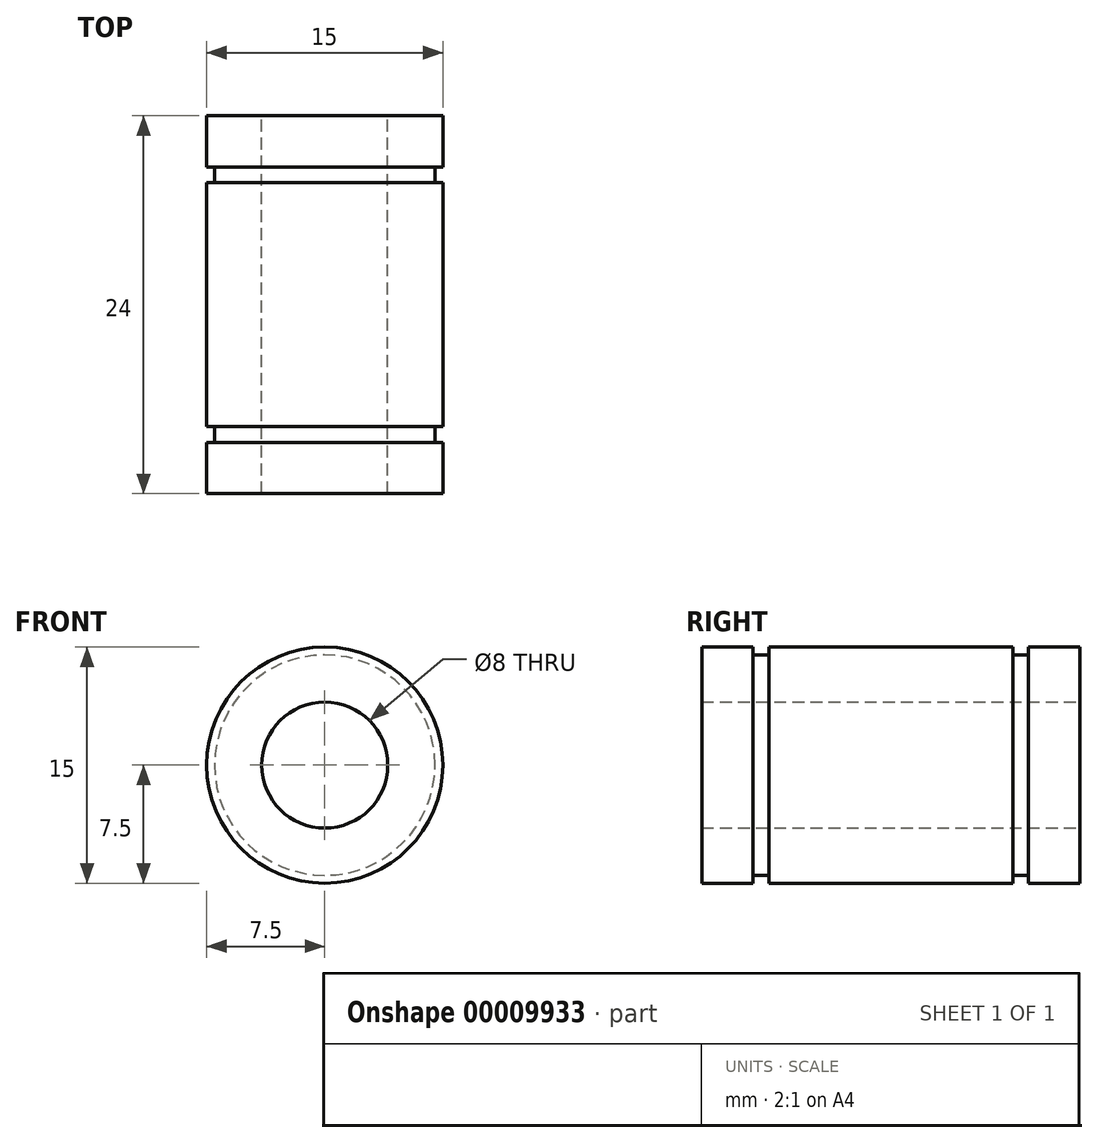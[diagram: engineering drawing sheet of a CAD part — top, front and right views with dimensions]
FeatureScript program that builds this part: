
annotation { "Feature Type Name" : "Feature", "Feature Type Description" : "" }
export const myFeature = defineFeature(function(context is Context, id is Id, definition is map)
    precondition{}
    {
        {
            var Q0;
            Q0=qCreatedBy(makeId("Front.planeOp"),FACE);
            var sketch = newSketch(context, id + "F0", { "sketchPlane" : qUnion([Q0])});
            skCircle(sketch, "E0", {"center": v(0, 0) * mm, "radius": 7.5 * mm});
            skCircle(sketch, "E1", {"center": v(0, 0) * mm, "radius": 4 * mm});
            skSolve(sketch);
        }
        {
            var Q0;
            Q0=qSketchRegion(id+"F0",true);
            extrude(context, id + "F1", {"entities" : qUnion([Q0]), "depth" : 3.25 * mm});
        }
        {
            var Q0;
            Q0=makeQuery(id+"F1.opExtrude","CAP_FACE",FACE,{"disambiguationData":[OSD([sQuery(id+"F0.wireOp",EDGE,"E0"),sQuery(id+"F0.wireOp",EDGE,"E1")])],"isStart":false});
            var sketch = newSketch(context, id + "F2", { "sketchPlane" : qUnion([Q0])});
            skCircle(sketch, "E2", {"center": v(0, 0) * mm, "radius": 7 * mm});
            skSolve(sketch);
        }
        {
            var Q0;
            Q0=makeQuery(id+"F2.imprint","IMPRINT",FACE,{"disambiguationData":[TD([[makeQuery(id+"F2.imprint","IMPRINT",EDGE,{"derivedFrom":sQuery(id+"F2.wireOp",EDGE,"E2")}),1.0]])]});
            extrude(context, id + "F3", {"entities" : qUnion([Q0]), "operationType" : NewBodyOperationType.ADD, "depth" : 1 * mm});
        }
        {
            var Q0;
            Q0=makeQuery(id+"F3.opExtrude","CAP_FACE",FACE,{"disambiguationData":[OSD([sQuery(id+"F0.wireOp",EDGE,"E1"),sQuery(id+"F2.wireOp",EDGE,"E2")])],"isStart":false});
            var sketch = newSketch(context, id + "F4", { "sketchPlane" : qUnion([Q0])});
            skCircle(sketch, "E3.0", {"center": v(0, 0) * mm, "radius": 7.5 * mm});
            skSolve(sketch);
        }
        {
            var Q0;
            Q0=makeQuery(id+"F4.imprint","IMPRINT",FACE,{"disambiguationData":[TD([[makeQuery(id+"F4.imprint","IMPRINT",EDGE,{"derivedFrom":makeQuery(id+"F3.opExtrude","CAP_EDGE",EDGE,{"disambiguationData":[OSD([sQuery(id+"F2.wireOp",EDGE,"E2")])],"isStart":false})}),1.0]])]});
            var Q1;
            Q1=makeQuery(id+"F4.imprint","IMPRINT",FACE,{"disambiguationData":[TD([[makeQuery(id+"F4.imprint","IMPRINT",EDGE,{"derivedFrom":sQuery(id+"F4.wireOp",EDGE,"E3.0")}),1.0]])]});
            extrude(context, id + "F5", {"entities" : qUnion([Q0, Q1]), "operationType" : NewBodyOperationType.ADD, "depth" : 15.5 * mm});
        }
        {
            var Q0;
            Q0=makeQuery(id+"F5.opExtrude","CAP_FACE",FACE,{"disambiguationData":[OSD([sQuery(id+"F0.wireOp",EDGE,"E1"),sQuery(id+"F4.wireOp",EDGE,"E3.0")])],"isStart":false});
            var sketch = newSketch(context, id + "F6", { "sketchPlane" : qUnion([Q0])});
            skCircle(sketch, "E4.0", {"center": v(0, 0) * mm, "radius": 7 * mm});
            skSolve(sketch);
        }
        {
            var Q0;
            Q0=makeQuery(id+"F6.imprint","IMPRINT",FACE,{"disambiguationData":[TD([[makeQuery(id+"F6.imprint","IMPRINT",EDGE,{"derivedFrom":sQuery(id+"F6.wireOp",EDGE,"E4.0")}),1.0]])]});
            extrude(context, id + "F7", {"entities" : qUnion([Q0]), "operationType" : NewBodyOperationType.ADD, "depth" : 1 * mm});
        }
        {
            var Q0;
            Q0=makeQuery(id+"F7.opExtrude","CAP_FACE",FACE,{"disambiguationData":[OSD([sQuery(id+"F0.wireOp",EDGE,"E1"),sQuery(id+"F6.wireOp",EDGE,"E4.0")])],"isStart":false});
            var sketch = newSketch(context, id + "F8", { "sketchPlane" : qUnion([Q0])});
            skCircle(sketch, "E5.0", {"center": v(0, 0) * mm, "radius": 7.5 * mm});
            skSolve(sketch);
        }
        {
            var Q0;
            Q0=makeQuery(id+"F8.imprint","IMPRINT",FACE,{"disambiguationData":[TD([[makeQuery(id+"F8.imprint","IMPRINT",EDGE,{"derivedFrom":sQuery(id+"F8.wireOp",EDGE,"E5.0")}),1.0]])]});
            var Q1;
            Q1=makeQuery(id+"F8.imprint","IMPRINT",FACE,{"disambiguationData":[TD([[makeQuery(id+"F8.imprint","IMPRINT",EDGE,{"derivedFrom":makeQuery(id+"F7.opExtrude","CAP_EDGE",EDGE,{"disambiguationData":[OSD([sQuery(id+"F6.wireOp",EDGE,"E4.0")])],"isStart":false})}),1.0]])]});
            extrude(context, id + "F9", {"entities" : qUnion([Q0, Q1]), "operationType" : NewBodyOperationType.ADD, "depth" : 3.25 * mm});
        }
    });
